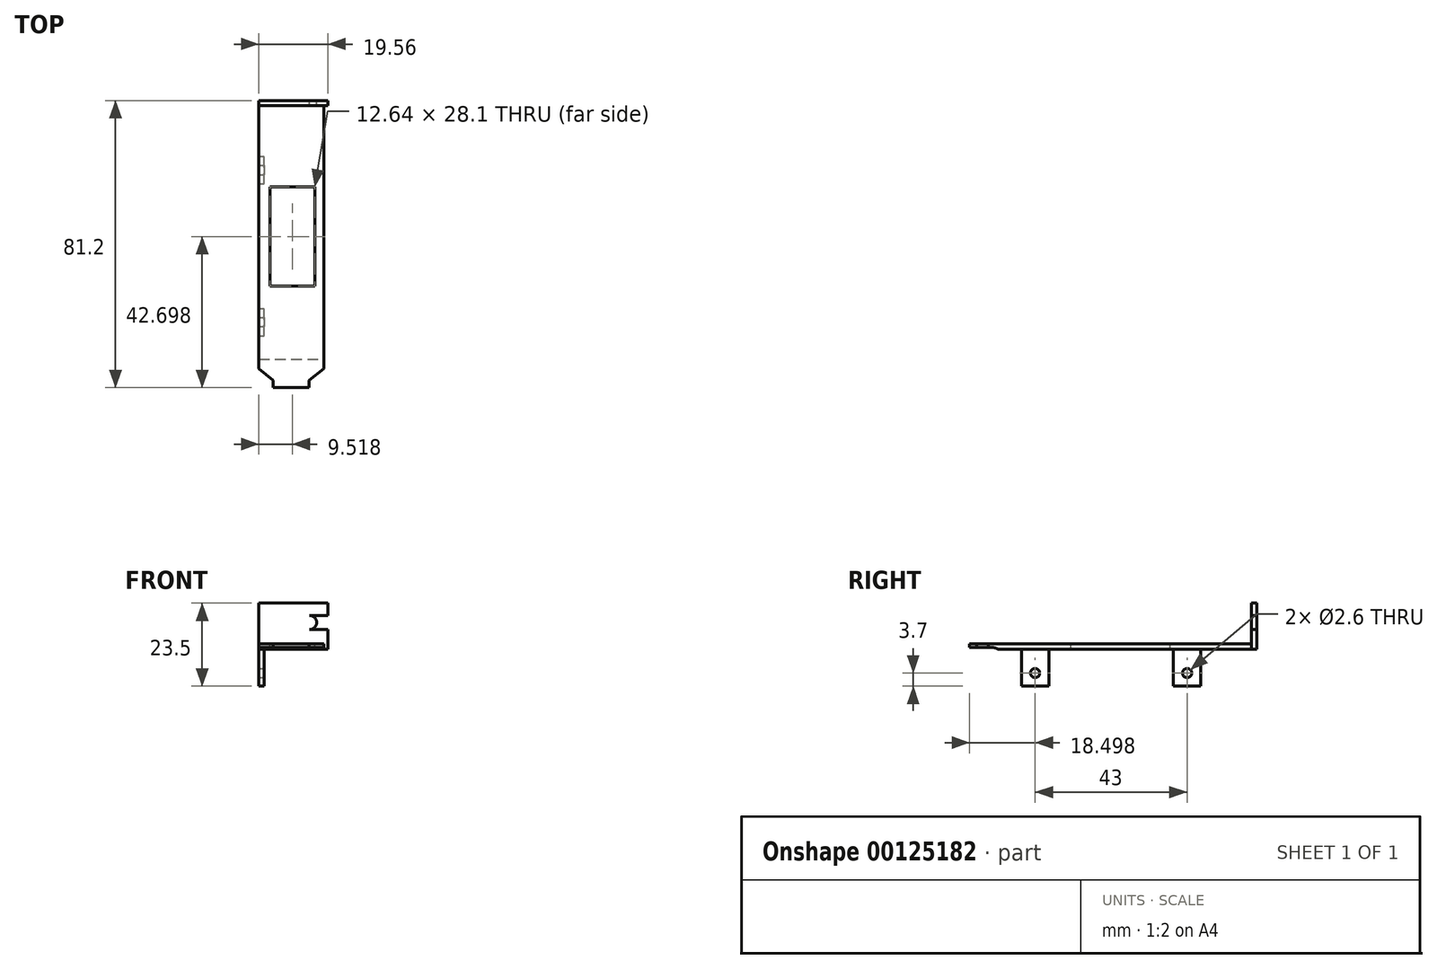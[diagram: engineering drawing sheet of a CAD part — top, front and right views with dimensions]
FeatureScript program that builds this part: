
annotation { "Feature Type Name" : "Feature", "Feature Type Description" : "" }
export const myFeature = defineFeature(function(context is Context, id is Id, definition is map)
    precondition{}
    {
        {
            var Q0;
            Q0=qCreatedBy(makeId("Top.planeOp"),FACE);
            var sketch = newSketch(context, id + "F0", { "sketchPlane" : qUnion([Q0])});
            skLineSegment(sketch, "E0.bottom", {"start": v(-5.44, 49.64) * mm, "end": v(12.96, 49.64) * mm});
            skLineSegment(sketch, "E0.left", {"start": v(-5.44, 49.64) * mm, "end": v(-5.44, -26.3) * mm});
            skLineSegment(sketch, "E0.right", {"start": v(12.96, 49.64) * mm, "end": v(12.96, -26.3) * mm});
            skPoint(sketch, "E0.middle", {"position": v(0, 0) * mm});
            skLineSegment(sketch, "E1", {"start": v(-1.34, -29.56) * mm, "end": v(-5.44, -26.3) * mm});
            skLineSegment(sketch, "E2", {"start": v(12.96, -26.3) * mm, "end": v(8.86, -29.56) * mm});
            skLineSegment(sketch, "E3", {"start": v(-1.34, -29.56) * mm, "end": v(8.86, -29.56) * mm});
            skLineSegment(sketch, "E4", {"start": v(-1.34, -29.56) * mm, "end": v(-1.34, -31.56) * mm});
            skLineSegment(sketch, "E5", {"start": v(-1.34, -31.56) * mm, "end": v(8.86, -31.56) * mm});
            skLineSegment(sketch, "E6", {"start": v(8.86, -31.56) * mm, "end": v(8.86, -29.56) * mm});
            skPoint(sketch, "E7.middle", {"position": v(4.18, 5.9) * mm});
            skSolve(sketch);
        }
        {
            var Q0;
            Q0=qSketchRegion(id+"F0",true);
            extrude(context, id + "F1", {"entities" : qUnion([Q0]), "depth" : 1.5 * mm});
        }
        {
            var Q0;
            Q0=makeQuery(id+"F1.opExtrude","CAP_FACE",FACE,{"disambiguationData":[OSD([sQuery(id+"F0.wireOp",EDGE,"E0.bottom"),sQuery(id+"F0.wireOp",EDGE,"E0.left"),sQuery(id+"F0.wireOp",EDGE,"E0.right"),sQuery(id+"F0.wireOp",EDGE,"E1"),sQuery(id+"F0.wireOp",EDGE,"E2"),sQuery(id+"F0.wireOp",EDGE,"E4"),sQuery(id+"F0.wireOp",EDGE,"E5"),sQuery(id+"F0.wireOp",EDGE,"E6")])],"isStart":false});
            var sketch = newSketch(context, id + "F2", { "sketchPlane" : qUnion([Q0])});
            skLineSegment(sketch, "E8", {"start": v(-2.24, 25.19) * mm, "end": v(-2.24, -2.91) * mm});
            skLineSegment(sketch, "E9", {"start": v(-2.24, -2.91) * mm, "end": v(10.4, -2.91) * mm});
            skLineSegment(sketch, "E10", {"start": v(10.4, -2.91) * mm, "end": v(10.4, 25.19) * mm});
            skLineSegment(sketch, "E11", {"start": v(10.4, 25.19) * mm, "end": v(-2.24, 25.19) * mm});
            skLineSegment(sketch, "E12.0", {"start": v(-5.44, 49.64) * mm, "end": v(-5.44, -26.3) * mm});
            skSolve(sketch);
        }
        {
            var Q0;
            Q0=makeQuery(id+"F2.imprint","IMPRINT",FACE,{"disambiguationData":[TD([[makeQuery(id+"F2.imprint","IMPRINT",EDGE,{"derivedFrom":sQuery(id+"F2.wireOp",EDGE,"E8")}),1.0]])]});
            extrude(context, id + "F3", {"entities" : qUnion([Q0]), "operationType" : NewBodyOperationType.REMOVE, "oppositeDirection" : true, "depth" : 25 * mm});
        }
        {
            var Q0;
            Q0=makeQuery(id+"F1.opExtrude","CAP_FACE",FACE,{"disambiguationData":[OSD([sQuery(id+"F0.wireOp",EDGE,"E0.bottom"),sQuery(id+"F0.wireOp",EDGE,"E0.left"),sQuery(id+"F0.wireOp",EDGE,"E0.right"),sQuery(id+"F0.wireOp",EDGE,"E1"),sQuery(id+"F0.wireOp",EDGE,"E2"),sQuery(id+"F0.wireOp",EDGE,"E4"),sQuery(id+"F0.wireOp",EDGE,"E5"),sQuery(id+"F0.wireOp",EDGE,"E6")])],"isStart":true});
            var sketch = newSketch(context, id + "F4", { "sketchPlane" : qUnion([Q0])});
            skLineSegment(sketch, "E13", {"start": v(-3.94, 26.3) * mm, "end": v(-3.94, -49.64) * mm});
            skLineSegment(sketch, "E14", {"start": v(-3.94, 26.3) * mm, "end": v(-5.44, 26.3) * mm});
            skPoint(sketch, "E15.0", {"position": v(-5.44, -49.64) * mm});
            skLineSegment(sketch, "E16.0", {"start": v(-5.44, -49.64) * mm, "end": v(-5.44, 26.3) * mm});
            skLineSegment(sketch, "E17", {"start": v(-3.94, -49.64) * mm, "end": v(-5.44, -49.64) * mm});
            skLineSegment(sketch, "E18", {"start": v(-5.44, 26.3) * mm, "end": v(-3.94, 26.3) * mm});
            skSolve(sketch);
        }
        {
            var Q0;
            Q0=makeQuery(id+"F4.imprint","IMPRINT",FACE,{"disambiguationData":[TD([[makeQuery(id+"F4.imprint","IMPRINT",EDGE,{"derivedFrom":sQuery(id+"F4.wireOp",EDGE,"E13")}),-1.0]])]});
            extrude(context, id + "F5", {"entities" : qUnion([Q0]), "operationType" : NewBodyOperationType.ADD, "depth" : 10.5 * mm});
        }
        {
            var Q0;
            Q0=makeQuery(id+"F5.opExtrude","SWEPT_FACE",FACE,{"disambiguationData":[OSD([sQuery(id+"F4.wireOp",EDGE,"E13")])]});
            var sketch = newSketch(context, id + "F6", { "sketchPlane" : qUnion([Q0])});
            skCircle(sketch, "E19", {"center": v(-13.06, -6.8) * mm, "radius": 1.3 * mm});
            skCircle(sketch, "E20", {"center": v(29.94, -6.8) * mm, "radius": 1.3 * mm});
            skLineSegment(sketch, "E21", {"start": v(-13.06, -6.8) * mm, "end": v(29.94, -6.8) * mm, "construction": true});
            skLineSegment(sketch, "E22", {"start": v(-16.94, -10.5) * mm, "end": v(-16.94, 0) * mm});
            skLineSegment(sketch, "E23", {"start": v(-16.94, -10.5) * mm, "end": v(-9.19, -10.5) * mm});
            skLineSegment(sketch, "E24", {"start": v(-9.19, 0) * mm, "end": v(-9.19, -10.5) * mm});
            skLineSegment(sketch, "E25", {"start": v(26.06, -10.5) * mm, "end": v(26.06, 0) * mm});
            skLineSegment(sketch, "E26", {"start": v(26.06, -10.5) * mm, "end": v(33.81, -10.5) * mm});
            skLineSegment(sketch, "E27", {"start": v(33.81, 0) * mm, "end": v(33.81, -10.5) * mm});
            skSolve(sketch);
        }
        {
            var Q0;
            {var subQ0=sQuery(id+"F6.wireOp",EDGE,"E24");Q0=makeQuery(id+"F6.imprint","IMPRINT",FACE,{"disambiguationData":[TD([[makeQuery(id+"F6.imprint","IMPRINT",EDGE,{"derivedFrom":subQ0}),1.0]])]});}
            var Q1;
            Q1=makeQuery(id+"F6.imprint","IMPRINT",FACE,{"disambiguationData":[TD([[makeQuery(id+"F6.imprint","IMPRINT",EDGE,{"derivedFrom":sQuery(id+"F6.wireOp",EDGE,"E19")}),1.0]])]});
            var Q2;
            Q2=makeQuery(id+"F6.imprint","IMPRINT",FACE,{"disambiguationData":[TD([[makeQuery(id+"F6.imprint","IMPRINT",EDGE,{"derivedFrom":sQuery(id+"F6.wireOp",EDGE,"E20")}),1.0]])]});
            var Q3;
            {var subQ3=sQuery(id+"F6.wireOp",EDGE,"E27");Q3=makeQuery(id+"F6.imprint","IMPRINT",FACE,{"disambiguationData":[TD([[makeQuery(id+"F6.imprint","IMPRINT",EDGE,{"derivedFrom":subQ3}),1.0]])]});}
            var Q4;
            {var subQ0=sQuery(id+"F6.wireOp",EDGE,"E22");Q4=makeQuery(id+"F6.imprint","IMPRINT",FACE,{"disambiguationData":[TD([[makeQuery(id+"F6.imprint","IMPRINT",EDGE,{"derivedFrom":subQ0}),1.0]])]});}
            extrude(context, id + "F7", {"entities" : qUnion([Q0, Q1, Q2, Q3, Q4]), "operationType" : NewBodyOperationType.REMOVE, "oppositeDirection" : true, "depth" : 25 * mm});
        }
        {
            var Q0;
            {var subQ0=sQuery(id+"F4.wireOp",EDGE,"E13");var subQ1=makeQuery(id+"F5.opExtrude","CAP_EDGE",EDGE,{"disambiguationData":[OSD([subQ0])],"isStart":true});var subQ2=sQuery(id+"F0.wireOp",EDGE,"E0.bottom");Q0=makeQuery(id+"F7.boolean.opBoolean","MERGE",FACE,{"derivedFrom":[makeQuery(id+"F1.opExtrude","CAP_FACE",FACE,{"disambiguationData":[OSD([subQ2,sQuery(id+"F0.wireOp",EDGE,"E0.left"),sQuery(id+"F0.wireOp",EDGE,"E0.right"),sQuery(id+"F0.wireOp",EDGE,"E1"),sQuery(id+"F0.wireOp",EDGE,"E2"),sQuery(id+"F0.wireOp",EDGE,"E4"),sQuery(id+"F0.wireOp",EDGE,"E5"),sQuery(id+"F0.wireOp",EDGE,"E6")])],"isStart":true}),makeQuery(id+"F7.opExtrude","SWEPT_FACE",FACE,{"disambiguationData":[OSD([subQ0]),TDD([makeQuery(id+"F6.imprint","IMPRINT",EDGE,{"disambiguationData":[TD([[makeQuery(id+"F6.imprint","INTERSECT",VERTEX,{"derivedFrom":[subQ1,sQuery(id+"F6.wireOp",EDGE,"E22")]}),1.0]])],"derivedFrom":subQ1})])]}),makeQuery(id+"F7.opExtrude","SWEPT_FACE",FACE,{"disambiguationData":[OSD([subQ0]),TDD([makeQuery(id+"F6.imprint","IMPRINT",EDGE,{"disambiguationData":[TD([[makeQuery(id+"F6.imprint","INTERSECT",VERTEX,{"derivedFrom":[subQ1,sQuery(id+"F6.wireOp",EDGE,"E27")]}),-1.0]])],"derivedFrom":subQ1})])]}),makeQuery(id+"F7.opExtrude","SWEPT_FACE",FACE,{"disambiguationData":[OSD([subQ0]),TDD([makeQuery(id+"F6.imprint","IMPRINT",EDGE,{"disambiguationData":[TD([[makeQuery(id+"F6.imprint","INTERSECT",VERTEX,{"derivedFrom":[subQ1,sQuery(id+"F6.wireOp",EDGE,"E24")]}),-1.0]])],"derivedFrom":subQ1})])]})]});}
            var sketch = newSketch(context, id + "F8", { "sketchPlane" : qUnion([Q0])});
            skLineSegment(sketch, "E28", {"start": v(-8.88, 23.56) * mm, "end": v(16.4, 23.56) * mm});
            skSolve(sketch);
        }
        {
            var Q0;
            {var subQ0=sQuery(id+"F8.wireOp",EDGE,"E28");Q0=makeQuery(id+"F8.imprint","IMPRINT",FACE,{"disambiguationData":[TD([[makeQuery(id+"F8.imprint","IMPRINT",EDGE,{"derivedFrom":subQ0}),1.0]])]});}
            extrude(context, id + "F9", {"entities" : qUnion([Q0]), "operationType" : NewBodyOperationType.REMOVE, "oppositeDirection" : true, "depth" : .50 * mm});
        }
        {
            var Q0;
            Q0=makeQuery(id+"F9.boolean.opBoolean","COPY",EDGE,{"derivedFrom":makeQuery(id+"F9.opExtrude","CAP_EDGE",EDGE,{"disambiguationData":[OSD([sQuery(id+"F8.wireOp",EDGE,"E28")])],"isStart":false})});
            fillet(context, id + "F10", {"entities" : qUnion([Q0]), "radius" : 5 * mm, "tangentPropagation" : true, "allowEdgeOverflow" : false});
        }
        {
            var Q0;
            Q0=makeQuery(id+"F1.opExtrude","CAP_FACE",FACE,{"disambiguationData":[OSD([sQuery(id+"F0.wireOp",EDGE,"E0.bottom"),sQuery(id+"F0.wireOp",EDGE,"E0.left"),sQuery(id+"F0.wireOp",EDGE,"E0.right"),sQuery(id+"F0.wireOp",EDGE,"E1"),sQuery(id+"F0.wireOp",EDGE,"E2"),sQuery(id+"F0.wireOp",EDGE,"E4"),sQuery(id+"F0.wireOp",EDGE,"E5"),sQuery(id+"F0.wireOp",EDGE,"E6")])],"isStart":false});
            var sketch = newSketch(context, id + "F11", { "sketchPlane" : qUnion([Q0])});
            skLineSegment(sketch, "E29", {"start": v(-5.44, 48.14) * mm, "end": v(12.96, 48.14) * mm});
            skLineSegment(sketch, "E30", {"start": v(12.96, 48.14) * mm, "end": v(14.12, 48.14) * mm});
            skLineSegment(sketch, "E31", {"start": v(14.12, 48.14) * mm, "end": v(14.12, 49.64) * mm});
            skLineSegment(sketch, "E32", {"start": v(14.12, 49.64) * mm, "end": v(12.96, 49.64) * mm});
            skSolve(sketch);
        }
        {
            var Q0;
            {var subQ0=sQuery(id+"F11.wireOp",EDGE,"E29");Q0=makeQuery(id+"F11.imprint","IMPRINT",FACE,{"disambiguationData":[TD([[makeQuery(id+"F11.imprint","IMPRINT",EDGE,{"derivedFrom":subQ0}),1.0]])]});}
            var Q1;
            {var subQ0=sQuery(id+"F11.wireOp",EDGE,"E30");Q1=makeQuery(id+"F11.imprint","IMPRINT",FACE,{"disambiguationData":[TD([[makeQuery(id+"F11.imprint","IMPRINT",EDGE,{"derivedFrom":subQ0}),1.0]])]});}
            extrude(context, id + "F12", {"entities" : qUnion([Q0, Q1]), "operationType" : NewBodyOperationType.ADD, "depth" : 11.5 * mm});
        }
        {
            var Q0;
            {var subQ0=sQuery(id+"F0.wireOp",EDGE,"E0.bottom");Q0=makeQuery(id+"F12.boolean.opBoolean","MERGE",FACE,{"derivedFrom":[makeQuery(id+"F1.opExtrude","SWEPT_FACE",FACE,{"disambiguationData":[OSD([subQ0])]}),makeQuery(id+"F12.opExtrude","SWEPT_FACE",FACE,{"disambiguationData":[OSD([subQ0])]})]});}
            var sketch = newSketch(context, id + "F13", { "sketchPlane" : qUnion([Q0])});
            skLineSegment(sketch, "E33.0", {"start": v(5.44, 13) * mm, "end": v(5.44, 0) * mm});
            skLineSegment(sketch, "E33.1", {"start": v(5.44, 0) * mm, "end": v(-12.96, 0) * mm});
            skLineSegment(sketch, "E34.0", {"start": v(5.44, 13) * mm, "end": v(5.44, 13) * mm});
            skLineSegment(sketch, "E35.0", {"start": v(-12.96, 1.5) * mm, "end": v(-12.96, 1.5) * mm});
            skLineSegment(sketch, "E36", {"start": v(-3.76, 0) * mm, "end": v(-4.34, 13) * mm, "construction": true});
            skLineSegment(sketch, "E37.MirrorCS", {"start": v(-8.96, 5.5) * mm, "end": v(-12.96, 5.5) * mm});
            skLineSegment(sketch, "E38.MirrorCS", {"start": v(-8.96, 9.5) * mm, "end": v(-12.96, 9.5) * mm});
            skCircle(sketch, "E39.MirrorC", {"center": v(-8.96, 7.5) * mm, "radius": 2 * mm});
            skLineSegment(sketch, "E40", {"start": v(-12.96, 9.5) * mm, "end": v(-14.12, 9.5) * mm});
            skLineSegment(sketch, "E41", {"start": v(-12.96, 5.5) * mm, "end": v(-14.12, 5.5) * mm});
            skSolve(sketch);
        }
        {
            var Q0;
            {var subQ0=sQuery(id+"F13.wireOp",EDGE,"E39.MirrorC");var subQ1=makeQuery(id+"F13.imprint","INTERSECT",VERTEX,{"derivedFrom":[sQuery(id+"F13.wireOp",EDGE,"E37.MirrorCS"),subQ0]});Q0=makeQuery(id+"F13.imprint","IMPRINT",FACE,{"disambiguationData":[TD([[makeQuery(id+"F13.imprint","IMPRINT",EDGE,{"disambiguationData":[TD([[subQ1,1.0]])],"derivedFrom":subQ0}),-1.0]])]});}
            var Q1;
            {var subQ0=sQuery(id+"F13.wireOp",EDGE,"E37.MirrorCS");Q1=makeQuery(id+"F13.imprint","IMPRINT",FACE,{"disambiguationData":[TD([[makeQuery(id+"F13.imprint","IMPRINT",EDGE,{"derivedFrom":subQ0}),-1.0]])]});}
            var Q2;
            Q2=makeQuery(id+"F12.opExtrude","SWEPT_FACE",FACE,{"disambiguationData":[OSD([sQuery(id+"F11.wireOp",EDGE,"E29")])]});
            extrude(context, id + "F14", {"entities" : qUnion([Q0, Q1]), "operationType" : NewBodyOperationType.REMOVE, "endBound" : BoundingType.UP_TO_SURFACE, "oppositeDirection" : true, "endBoundEntityFace" : qUnion([Q2]), "depth" : 25 * mm});
        }
        {
            var Q0;
            Q0=makeQuery(id+"F12.opExtrude","CAP_FACE",FACE,{"disambiguationData":[OSD([sQuery(id+"F0.wireOp",EDGE,"E0.bottom"),sQuery(id+"F0.wireOp",EDGE,"E0.left"),sQuery(id+"F11.wireOp",EDGE,"E29"),sQuery(id+"F11.wireOp",EDGE,"E30"),sQuery(id+"F11.wireOp",EDGE,"E31"),sQuery(id+"F11.wireOp",EDGE,"E32")])],"isStart":true});
            var Q1;
            {var subQ0=sQuery(id+"F4.wireOp",EDGE,"E13");var subQ1=makeQuery(id+"F5.opExtrude","CAP_EDGE",EDGE,{"disambiguationData":[OSD([subQ0])],"isStart":true});var subQ2=sQuery(id+"F0.wireOp",EDGE,"E0.bottom");Q1=makeQuery(id+"F7.boolean.opBoolean","MERGE",FACE,{"derivedFrom":[makeQuery(id+"F1.opExtrude","CAP_FACE",FACE,{"disambiguationData":[OSD([subQ2,sQuery(id+"F0.wireOp",EDGE,"E0.left"),sQuery(id+"F0.wireOp",EDGE,"E0.right"),sQuery(id+"F0.wireOp",EDGE,"E1"),sQuery(id+"F0.wireOp",EDGE,"E2"),sQuery(id+"F0.wireOp",EDGE,"E4"),sQuery(id+"F0.wireOp",EDGE,"E5"),sQuery(id+"F0.wireOp",EDGE,"E6")])],"isStart":true}),makeQuery(id+"F7.opExtrude","SWEPT_FACE",FACE,{"disambiguationData":[OSD([subQ0]),TDD([makeQuery(id+"F6.imprint","IMPRINT",EDGE,{"disambiguationData":[TD([[makeQuery(id+"F6.imprint","INTERSECT",VERTEX,{"derivedFrom":[subQ1,sQuery(id+"F6.wireOp",EDGE,"E22")]}),1.0]])],"derivedFrom":subQ1})])]}),makeQuery(id+"F7.opExtrude","SWEPT_FACE",FACE,{"disambiguationData":[OSD([subQ0]),TDD([makeQuery(id+"F6.imprint","IMPRINT",EDGE,{"disambiguationData":[TD([[makeQuery(id+"F6.imprint","INTERSECT",VERTEX,{"derivedFrom":[subQ1,sQuery(id+"F6.wireOp",EDGE,"E27")]}),-1.0]])],"derivedFrom":subQ1})])]}),makeQuery(id+"F7.opExtrude","SWEPT_FACE",FACE,{"disambiguationData":[OSD([subQ0]),TDD([makeQuery(id+"F6.imprint","IMPRINT",EDGE,{"disambiguationData":[TD([[makeQuery(id+"F6.imprint","INTERSECT",VERTEX,{"derivedFrom":[subQ1,sQuery(id+"F6.wireOp",EDGE,"E24")]}),-1.0]])],"derivedFrom":subQ1})])]})]});}
            extrude(context, id + "F15", {"entities" : qUnion([Q0]), "operationType" : NewBodyOperationType.ADD, "endBound" : BoundingType.UP_TO_SURFACE, "endBoundEntityFace" : qUnion([Q1]), "depth" : 25 * mm});
        }
    });
